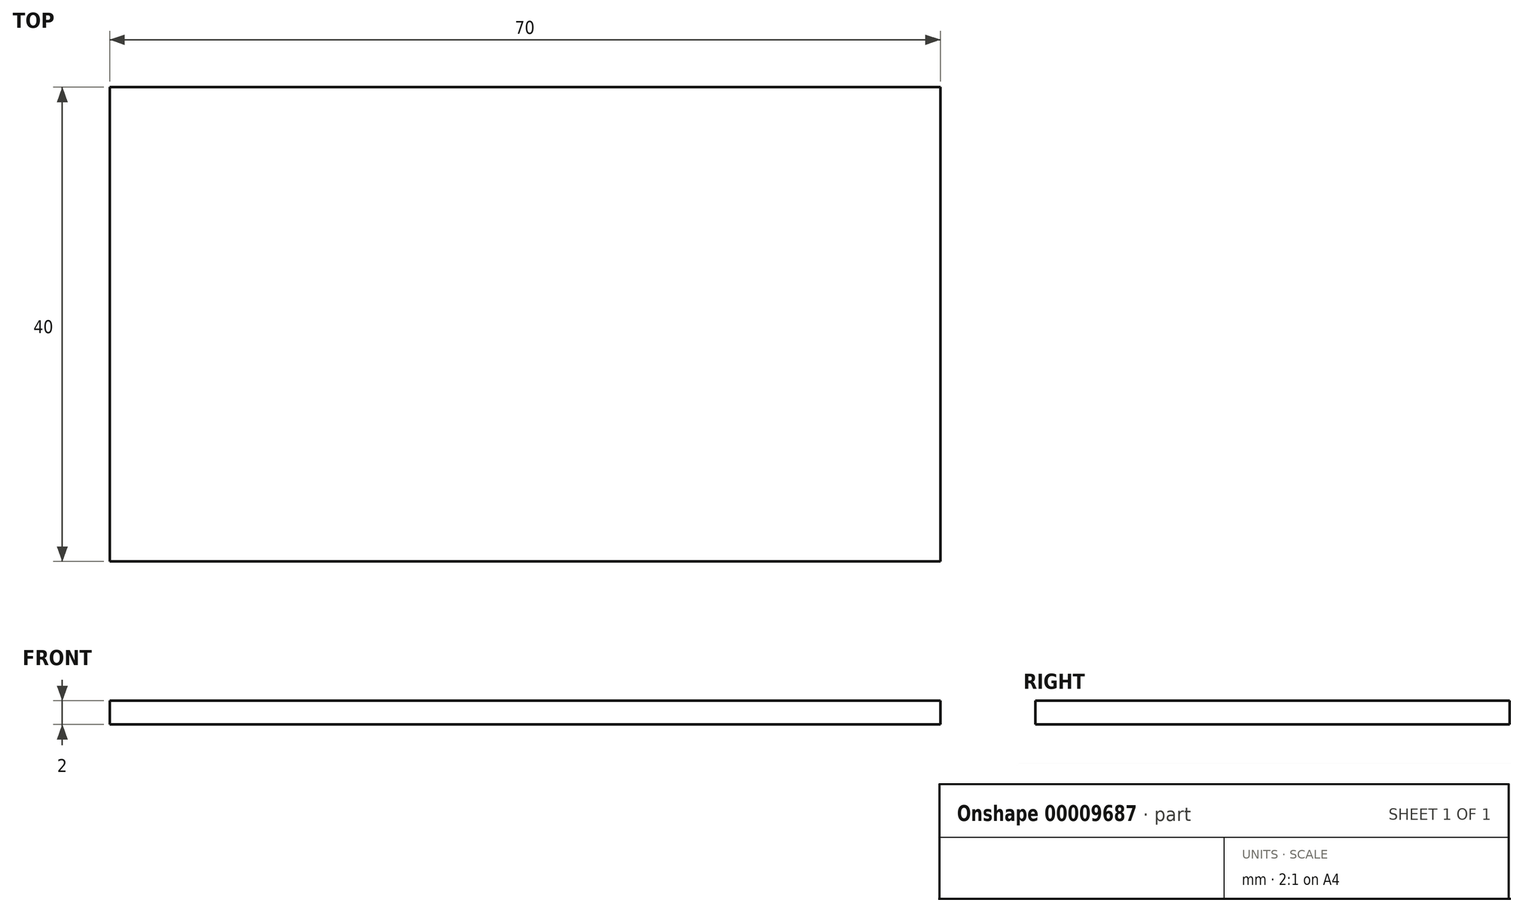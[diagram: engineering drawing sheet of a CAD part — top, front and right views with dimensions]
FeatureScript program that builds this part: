
annotation { "Feature Type Name" : "Feature", "Feature Type Description" : "" }
export const myFeature = defineFeature(function(context is Context, id is Id, definition is map)
    precondition{}
    {
        {
            var Q0;
            Q0=qCreatedBy(makeId("Top.planeOp"),FACE);
            var sketch = newSketch(context, id + "F0", { "sketchPlane" : qUnion([Q0])});
            skLineSegment(sketch, "E0.rect.bottom", {"start": v(-35, 20) * mm, "end": v(35, 20) * mm});
            skLineSegment(sketch, "E0.rect.top", {"start": v(-35, -20) * mm, "end": v(35, -20) * mm});
            skLineSegment(sketch, "E0.rect.left", {"start": v(-35, 20) * mm, "end": v(-35, -20) * mm});
            skLineSegment(sketch, "E0.rect.right", {"start": v(35, 20) * mm, "end": v(35, -20) * mm});
            skPoint(sketch, "E0.rect.middle", {"position": v(0, 0) * mm});
            skSolve(sketch);
        }
        {
            var Q0;
            Q0=qSketchRegion(id+"F0",true);
            extrude(context, id + "F1", {"entities" : qUnion([Q0]), "depth" : 2 * mm});
        }
    });
